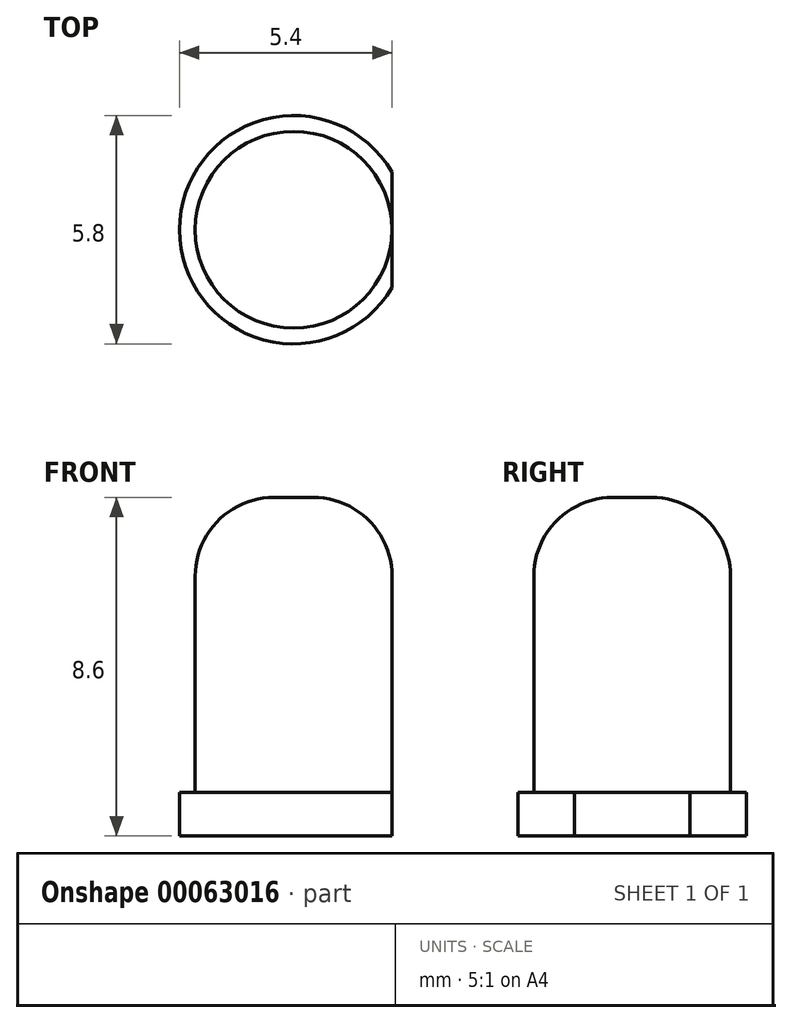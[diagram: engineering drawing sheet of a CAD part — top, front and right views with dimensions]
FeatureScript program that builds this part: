
annotation { "Feature Type Name" : "Feature", "Feature Type Description" : "" }
export const myFeature = defineFeature(function(context is Context, id is Id, definition is map)
    precondition{}
    {
        {
            var Q0;
            Q0=qCreatedBy(makeId("Top.planeOp"),FACE);
            var sketch = newSketch(context, id + "F2", { "sketchPlane" : qUnion([Q0])});
            skCircle(sketch, "E0", {"center": v(0, 0) * mm, "radius": 2.5 * mm});
            skSolve(sketch);
        }
        {
            var Q0;
            Q0=makeQuery(id+"F2.imprint","IMPRINT",FACE,{"disambiguationData":[TD([[makeQuery(id+"F2.imprint","IMPRINT",EDGE,{"derivedFrom":sQuery(id+"F2.wireOp",EDGE,"E0")}),1.0]])]});
            extrude(context, id + "F0", {"entities" : qUnion([Q0]), "depth" : 8.6 * mm});
        }
        {
            var Q0;
            Q0=qCreatedBy(makeId("Top.planeOp"),FACE);
            var sketch = newSketch(context, id + "F1", { "sketchPlane" : qUnion([Q0])});
            skCircle(sketch, "E1", {"center": v(0, 0) * mm, "radius": 2.9 * mm});
            skLineSegment(sketch, "E2", {"start": v(2.5, -1.47) * mm, "end": v(2.5, 1.47) * mm});
            skSolve(sketch);
        }
        {
            var Q0;
            {var subQ0=sQuery(id+"F1.wireOp",EDGE,"E2");Q0=makeQuery(id+"F1.imprint","IMPRINT",FACE,{"disambiguationData":[TD([[makeQuery(id+"F1.imprint","IMPRINT",EDGE,{"derivedFrom":subQ0}),1.0]])]});}
            extrude(context, id + "F3", {"entities" : qUnion([Q0]), "operationType" : NewBodyOperationType.ADD, "depth" : 1.1 * mm});
        }
        {
            var Q0;
            Q0=makeQuery(id+"F0.opExtrude","CAP_EDGE",EDGE,{"disambiguationData":[OSD([sQuery(id+"F2.wireOp",EDGE,"E0")])],"isStart":false});
            fillet(context, id + "F4", {"entities" : qUnion([Q0]), "radius" : 2 * mm, "tangentPropagation" : true, "allowEdgeOverflow" : false});
        }
    });
